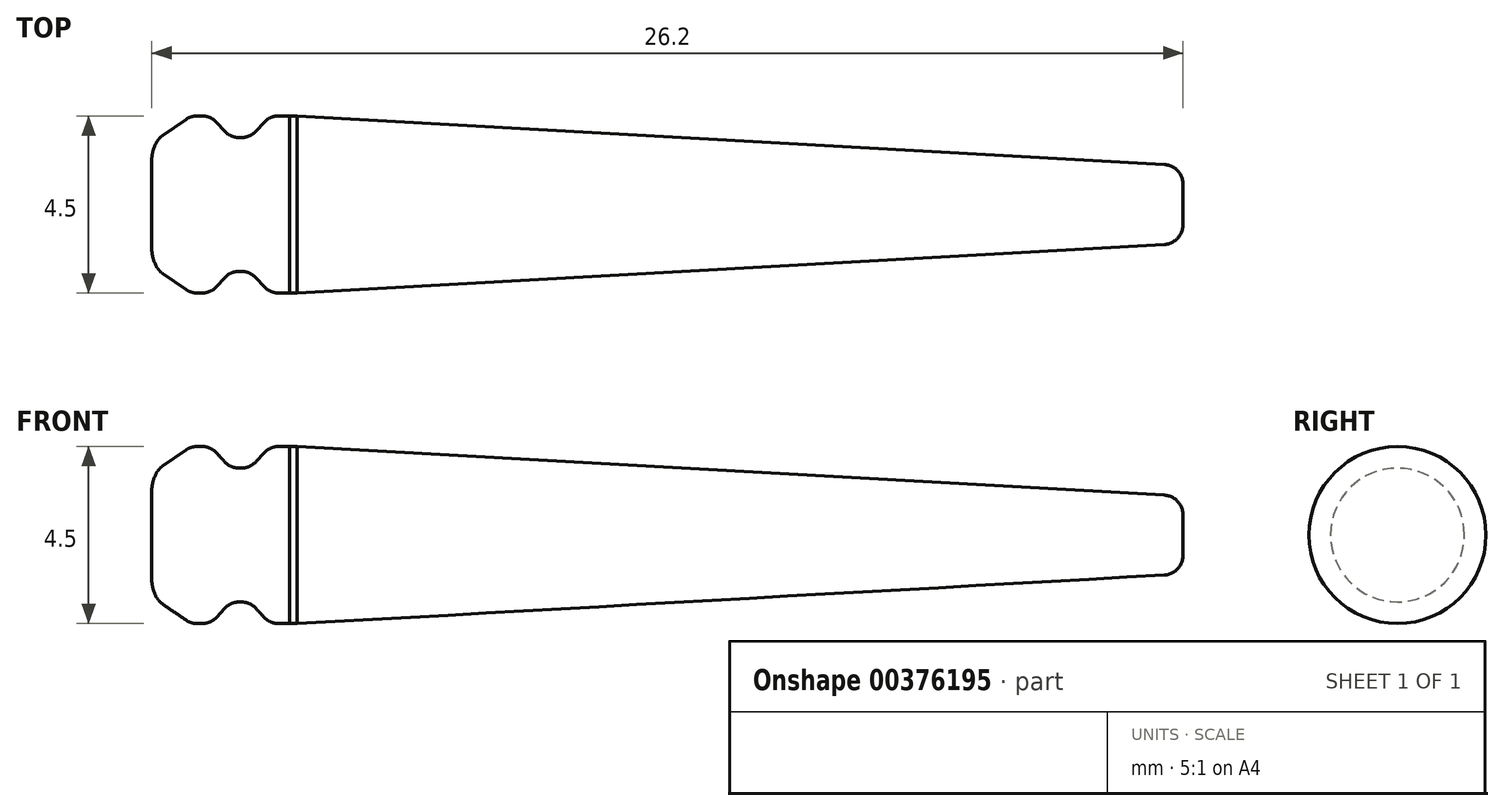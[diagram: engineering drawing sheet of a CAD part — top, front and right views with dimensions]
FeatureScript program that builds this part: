
annotation { "Feature Type Name" : "Feature", "Feature Type Description" : "" }
export const myFeature = defineFeature(function(context is Context, id is Id, definition is map)
    precondition{}
    {
        {
            var Q0;
            Q0=qCreatedBy(makeId("Right.planeOp"),FACE);
            var sketch = newSketch(context, id + "F0", { "sketchPlane" : qUnion([Q0])});
            skCircle(sketch, "E0", {"center": v(0, 0) * mm, "radius": 2.25 * mm});
            skSolve(sketch);
        }
        {
            var Q0;
            Q0 = qSketchRegion(id + "F0", true);
            extrude(context, id + "F1", {"entities" : qUnion([Q0]), "depth" : 0.5 * mm});
        }
        {
            var Q0;
            Q0=qCreatedBy(makeId("Right.planeOp"),FACE);
            var sketch = newSketch(context, id + "F2", { "sketchPlane" : qUnion([Q0])});
            skCircle(sketch, "E1", {"center": v(0, 0) * mm, "radius": 1.7 * mm});
            skSolve(sketch);
        }
        {
            var Q0;
            Q0 = qSketchRegion(id + "F2", true);
            extrude(context, id + "F3", {"entities" : qUnion([Q0]), "depth" : 1.5 * mm, "hasSecondDirection" : true, "secondDirectionOppositeDirection" : false, "secondDirectionDepth" : 1 * mm});
        }
        {
            var Q0;
            Q0=makeQuery(id+"F1.opExtrude","CAP_FACE",FACE,{"disambiguationData":[OSD([sQuery(id+"F0.wireOp",EDGE,"E0")])],"isStart":false});
            var Q1;
            Q1=makeQuery(id+"F3.opExtrude","CAP_FACE",FACE,{"disambiguationData":[OSD([sQuery(id+"F2.wireOp",EDGE,"E1")])],"isStart":true});
            loft(context, id + "F4", {"operationType" : NewBodyOperationType.ADD, "sheetProfilesArray" : [{ "sheetProfileEntities" : qUnion([Q0]) }, { "sheetProfileEntities" : qUnion([Q1]) }]});
        }
        {
            var Q0;
            Q0=qCreatedBy(makeId("Right.planeOp"),FACE);
            var sketch = newSketch(context, id + "F5", { "sketchPlane" : qUnion([Q0])});
            skCircle(sketch, "E2", {"center": v(0, 0) * mm, "radius": 2.25 * mm});
            skSolve(sketch);
        }
        {
            var Q0;
            Q0=makeQuery(id+"F5.imprint","IMPRINT",FACE,{"disambiguationData":[TD([[makeQuery(id+"F5.imprint","IMPRINT",EDGE,{"derivedFrom":sQuery(id+"F5.wireOp",EDGE,"E2")}),1.0]])]});
            extrude(context, id + "F6", {"entities" : qUnion([Q0]), "depth" : 2.5 * mm, "hasSecondDirection" : true, "secondDirectionOppositeDirection" : false, "secondDirectionDepth" : 2 * mm});
        }
        {
            var Q0;
            Q0=makeQuery(id+"F6.opExtrude","CAP_FACE",FACE,{"disambiguationData":[OSD([sQuery(id+"F5.wireOp",EDGE,"E2")])],"isStart":true});
            var Q1;
            Q1=makeQuery(id+"F3.opExtrude","CAP_FACE",FACE,{"disambiguationData":[OSD([sQuery(id+"F2.wireOp",EDGE,"E1")])],"isStart":false});
            loft(context, id + "F7", {"operationType" : NewBodyOperationType.ADD, "sheetProfilesArray" : [{ "sheetProfileEntities" : qUnion([Q0]) }, { "sheetProfileEntities" : qUnion([Q1]) }]});
        }
        {
            var Q0;
            Q0=makeQuery(id+"F4.opLoft","SWEPT_FACE",FACE,{"disambiguationData":[OSD([sQuery(id+"F0.wireOp",EDGE,"E0"),sQuery(id+"F2.wireOp",EDGE,"E1")])]});
            var Q1;
            Q1=makeQuery(id+"F7.opLoft","SWEPT_FACE",FACE,{"disambiguationData":[OSD([sQuery(id+"F2.wireOp",EDGE,"E1"),sQuery(id+"F5.wireOp",EDGE,"E2")])]});
            fillet(context, id + "F8", {"entities" : qUnion([Q0, Q1]), "radius" : 0.5 * mm, "tangentPropagation" : true, "allowEdgeOverflow" : false});
        }
        {
            var Q0;
            Q0=qCreatedBy(makeId("Right.planeOp"),FACE);
            var sketch = newSketch(context, id + "F9", { "sketchPlane" : qUnion([Q0])});
            skCircle(sketch, "E3", {"center": v(0, 0) * mm, "radius": 1.7 * mm});
            skSolve(sketch);
        }
        {
            var Q0;
            Q0 = qSketchRegion(id + "F9", true);
            extrude(context, id + "F10", {"entities" : qUnion([Q0]), "oppositeDirection" : true, "depth" : 1 * mm, "hasSecondDirection" : true, "secondDirectionOppositeDirection" : true, "secondDirectionDepth" : 0.8 * mm});
        }
        {
            var Q0;
            Q0=makeQuery(id+"F10.opExtrude","CAP_FACE",FACE,{"disambiguationData":[OSD([sQuery(id+"F9.wireOp",EDGE,"E3")])],"isStart":true});
            var Q1;
            Q1=makeQuery(id+"F1.opExtrude","CAP_FACE",FACE,{"disambiguationData":[OSD([sQuery(id+"F0.wireOp",EDGE,"E0")])],"isStart":true});
            loft(context, id + "F11", {"operationType" : NewBodyOperationType.ADD, "sheetProfilesArray" : [{ "sheetProfileEntities" : qUnion([Q0]) }, { "sheetProfileEntities" : qUnion([Q1]) }]});
        }
        {
            var Q0;
            Q0=makeQuery(id+"F10.opExtrude","CAP_EDGE",EDGE,{"disambiguationData":[OSD([sQuery(id+"F9.wireOp",EDGE,"E3")])],"isStart":false});
            fillet(context, id + "F12", {"entities" : qUnion([Q0]), "radius" : 1 * mm, "tangentPropagation" : true, "allowEdgeOverflow" : false});
        }
        {
            var Q0;
            Q0=makeQuery(id+"F11.opLoft","SWEPT_FACE",FACE,{"disambiguationData":[OSD([sQuery(id+"F0.wireOp",EDGE,"E0"),sQuery(id+"F9.wireOp",EDGE,"E3")])]});
            fillet(context, id + "F13", {"entities" : qUnion([Q0]), "radius" : .5 * mm, "tangentPropagation" : true, "allowEdgeOverflow" : false});
        }
        {
            var Q0;
            Q0=qCreatedBy(makeId("Right.planeOp"),FACE);
            var sketch = newSketch(context, id + "F14", { "sketchPlane" : qUnion([Q0])});
            skCircle(sketch, "E4", {"center": v(0, 0) * mm, "radius": 2.25 * mm});
            skSolve(sketch);
        }
        {
            var Q0;
            Q0 = qSketchRegion(id + "F14", true);
            extrude(context, id + "F15", {"entities" : qUnion([Q0]), "depth" : 2.7 * mm, "hasSecondDirection" : true, "secondDirectionOppositeDirection" : false, "secondDirectionDepth" : 2.5 * mm});
        }
        {
            var Q0;
            Q0=qCreatedBy(makeId("Right.planeOp"),FACE);
            var sketch = newSketch(context, id + "F16", { "sketchPlane" : qUnion([Q0])});
            skCircle(sketch, "E5", {"center": v(0, 0) * mm, "radius": 1 * mm});
            skSolve(sketch);
        }
        {
            var Q0;
            Q0=makeQuery(id+"F16.imprint","IMPRINT",FACE,{"disambiguationData":[TD([[makeQuery(id+"F16.imprint","IMPRINT",EDGE,{"derivedFrom":sQuery(id+"F16.wireOp",EDGE,"E5")}),1.0]])]});
            extrude(context, id + "F17", {"entities" : qUnion([Q0]), "depth" : 25.2 * mm, "hasSecondDirection" : true, "secondDirectionOppositeDirection" : false, "secondDirectionDepth" : 25 * mm});
        }
        {
            var Q0;
            Q0=makeQuery(id+"F15.opExtrude","CAP_FACE",FACE,{"disambiguationData":[OSD([sQuery(id+"F14.wireOp",EDGE,"E4")])],"isStart":false});
            var Q1;
            Q1=makeQuery(id+"F17.opExtrude","CAP_FACE",FACE,{"disambiguationData":[OSD([sQuery(id+"F16.wireOp",EDGE,"E5")])],"isStart":true});
            loft(context, id + "F18", {"operationType" : NewBodyOperationType.ADD, "sheetProfilesArray" : [{ "sheetProfileEntities" : qUnion([Q0]) }, { "sheetProfileEntities" : qUnion([Q1]) }]});
        }
        {
            var Q0;
            Q0=makeQuery(id+"F17.opExtrude","CAP_EDGE",EDGE,{"disambiguationData":[OSD([sQuery(id+"F16.wireOp",EDGE,"E5")])],"isStart":false});
            fillet(context, id + "F19", {"entities" : qUnion([Q0]), "radius" : 0.5 * mm, "tangentPropagation" : true, "allowEdgeOverflow" : false});
        }
    });
